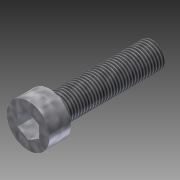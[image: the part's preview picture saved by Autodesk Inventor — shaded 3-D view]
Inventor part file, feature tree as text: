
AUTODESK INVENTOR PART (.ipt)
format: ipt  version: 2015 (Build 190159000, 159)  size: 101,888 bytes
history: native  units: mm
features: extrude x3, sketch x2, thread x1
ambient origin geometry x8: Origin, YZ Plane, XZ Plane, XY Plane, X Axis, Y Axis, Z Axis, Center Point
bodies: Solid1 (feature_tree)
feature tree (6):
  sketch  "Sketch1"  dims[d0=3.0mm d1=5.0mm]
  extrude  "Extrusion1"  Depth=5.0mm
  extrude  "Extrusion2"  Depth=2.5mm TaperAngle=0.0deg
  thread  "Thread1"  [1 undecoded]
  extrude  "Extrusion3"  Depth=2.0mm TaperAngle=0.0deg
  sketch  "Sketch2"  dims[d2=12.0mm d3=0.0mm d4=2.5mm d5=0.0mm d6=10.0mm d7=0.0mm d9=2.0mm d10=0.0mm]
note: 1 required parameter value undecoded (feature->parameter linkage not recoverable at this tier; creation-order binding heuristic only, values carry confidence <= 0.55)
